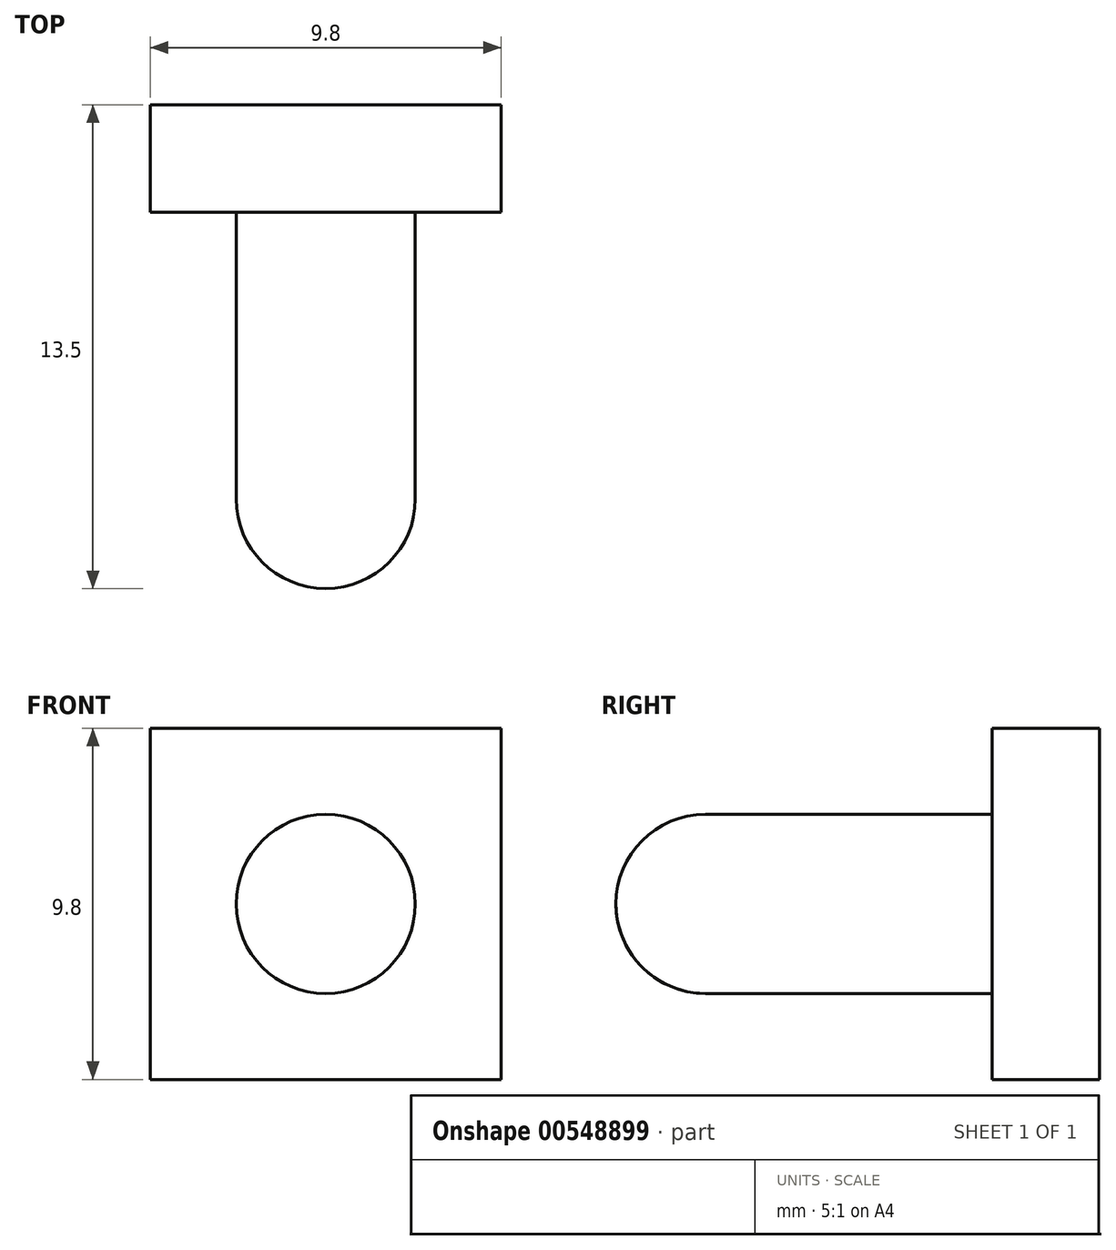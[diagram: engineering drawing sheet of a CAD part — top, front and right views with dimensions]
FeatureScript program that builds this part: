
annotation { "Feature Type Name" : "Feature", "Feature Type Description" : "" }
export const myFeature = defineFeature(function(context is Context, id is Id, definition is map)
    precondition{}
    {
        {
            var Q0;
            Q0=qCreatedBy(makeId("Front.planeOp"),FACE);
            var sketch = newSketch(context, id + "F0", { "sketchPlane" : qUnion([Q0])});
            skLineSegment(sketch, "E0.bottom", {"start": v(-4.9, 4.9) * mm, "end": v(4.9, 4.9) * mm});
            skLineSegment(sketch, "E0.top", {"start": v(-4.9, -4.9) * mm, "end": v(4.9, -4.9) * mm});
            skLineSegment(sketch, "E0.left", {"start": v(-4.9, 4.9) * mm, "end": v(-4.9, -4.9) * mm});
            skLineSegment(sketch, "E0.right", {"start": v(4.9, 4.9) * mm, "end": v(4.9, -4.9) * mm});
            skPoint(sketch, "E0.middle", {"position": v(0, 0) * mm});
            skCircle(sketch, "E1", {"center": v(0, 0) * mm, "radius": 2.5 * mm});
            skSolve(sketch);
        }
        {
            var Q0;
            Q0=makeQuery(id+"F0.imprint","IMPRINT",FACE,{"disambiguationData":[TD([[makeQuery(id+"F0.imprint","IMPRINT",EDGE,{"derivedFrom":sQuery(id+"F0.wireOp",EDGE,"E0.bottom")}),-1.0]])]});
            var Q1;
            Q1=makeQuery(id+"F0.imprint","IMPRINT",FACE,{"disambiguationData":[TD([[makeQuery(id+"F0.imprint","IMPRINT",EDGE,{"derivedFrom":sQuery(id+"F0.wireOp",EDGE,"E1")}),1.0]])]});
            extrude(context, id + "F1", {"entities" : qUnion([Q0, Q1]), "endBound" : BoundingType.SYMMETRIC, "oppositeDirection" : true, "depth" : 3 * mm, "offsetDistance" : 25 * mm});
        }
        {
            var Q0;
            Q0=makeQuery(id+"F0.imprint","IMPRINT",FACE,{"disambiguationData":[TD([[makeQuery(id+"F0.imprint","IMPRINT",EDGE,{"derivedFrom":sQuery(id+"F0.wireOp",EDGE,"E1")}),1.0]])]});
            var Q1;
            Q1=sQuery(id+"F0.wireOp",EDGE,"E1");
            extrude(context, id + "F2", {"entities" : qUnion([Q0]), "operationType" : NewBodyOperationType.ADD, "surfaceEntities" : qUnion([Q1]), "depth" : 12 * mm, "offsetDistance" : 25 * mm});
        }
        {
            var Q0;
            Q0=makeQuery(id+"F2.opExtrude","CAP_EDGE",EDGE,{"disambiguationData":[OSD([sQuery(id+"F0.wireOp",EDGE,"E1")])],"isStart":false});
            fillet(context, id + "F3", {"entities" : qUnion([Q0]), "radius" : 2.5 * mm, "tangentPropagation" : true, "allowEdgeOverflow" : false});
        }
    });
